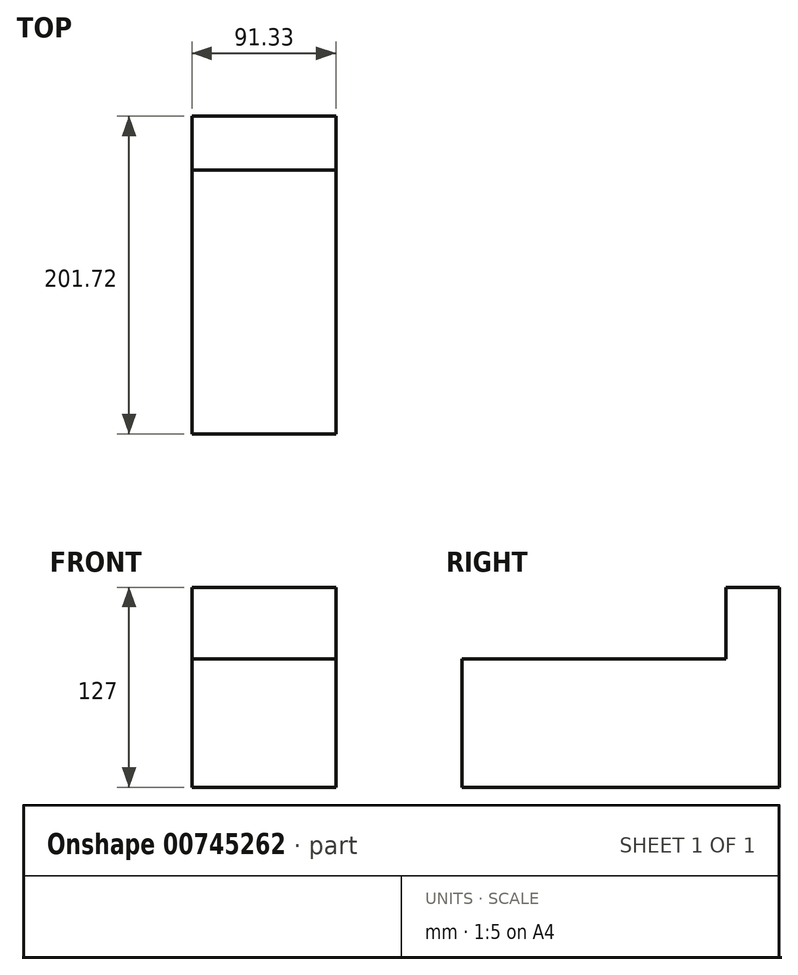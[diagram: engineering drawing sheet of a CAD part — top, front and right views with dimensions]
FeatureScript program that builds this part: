
annotation { "Feature Type Name" : "Feature", "Feature Type Description" : "" }
export const myFeature = defineFeature(function(context is Context, id is Id, definition is map)
    precondition{}
    {
        {
            var Q0;
            Q0=qCreatedBy(makeId("Top.planeOp"),FACE);
            var sketch = newSketch(context, id + "F0", { "sketchPlane" : qUnion([Q0])});
            skLineSegment(sketch, "E0.bottom", {"start": v(-55.85, 45.48) * mm, "end": v(35.48, 45.48) * mm});
            skLineSegment(sketch, "E0.top", {"start": v(-55.85, -52.1) * mm, "end": v(35.48, -52.1) * mm});
            skLineSegment(sketch, "E0.left", {"start": v(-55.85, 45.48) * mm, "end": v(-55.85, -52.1) * mm});
            skLineSegment(sketch, "E0.right", {"start": v(35.48, 45.48) * mm, "end": v(35.48, -52.1) * mm});
            skSolve(sketch);
        }
        {
            var Q0;
            Q0 = qSketchRegion(id + "F0", true);
            extrude(context, id + "F1", {"entities" : qUnion([Q0]), "depth" : 127 * mm, "offsetDistance" : 25.4 * mm});
        }
        {
            var Q0;
            Q0=makeQuery(id+"F1.opExtrude","SWEPT_FACE",FACE,{"disambiguationData":[OSD([sQuery(id+"F0.wireOp",EDGE,"E0.top")])]});
            var sketch = newSketch(context, id + "F2", { "sketchPlane" : qUnion([Q0])});
            skLineSegment(sketch, "E1.bottom", {"start": v(-55.85, 127) * mm, "end": v(35.48, 127) * mm});
            skLineSegment(sketch, "E1.top", {"start": v(-55.85, 81.4) * mm, "end": v(35.48, 81.4) * mm});
            skLineSegment(sketch, "E1.left", {"start": v(-55.85, 127) * mm, "end": v(-55.85, 81.4) * mm});
            skLineSegment(sketch, "E1.right", {"start": v(35.48, 127) * mm, "end": v(35.48, 81.4) * mm});
            skSolve(sketch);
        }
        {
            var Q0;
            Q0 = qSketchRegion(id + "F2", true);
            extrude(context, id + "F3", {"entities" : qUnion([Q0]), "operationType" : NewBodyOperationType.REMOVE, "oppositeDirection" : true, "depth" : 63.5 * mm, "offsetDistance" : 25.4 * mm});
        }
        {
            var Q0;
            Q0=makeQuery(id+"F1.opExtrude","SWEPT_FACE",FACE,{"disambiguationData":[OSD([sQuery(id+"F0.wireOp",EDGE,"E0.top")])]});
            extrude(context, id + "F4", {"entities" : qUnion([Q0]), "operationType" : NewBodyOperationType.ADD, "depth" : 25.4 * mm, "offsetDistance" : 25.4 * mm});
        }
        {
            var Q0;
            Q0=makeQuery(id+"F4.opExtrude","CAP_FACE",FACE,{"disambiguationData":[OSD([sQuery(id+"F0.wireOp",EDGE,"E0.top")])],"isStart":false});
            var sketch = newSketch(context, id + "F5", { "sketchPlane" : qUnion([Q0])});
            skSolve(sketch);
        }
        {
            var Q0;
            {var subQ0=sQuery(id+"F0.wireOp",EDGE,"E0.top");Q0=makeQuery(id+"F5.imprint","IMPRINT",FACE,{"disambiguationData":[TD([[makeQuery(id+"F5.imprint","IMPRINT",EDGE,{"derivedFrom":makeQuery(id+"F4.opExtrude","CAP_EDGE",EDGE,{"disambiguationData":[OSD([subQ0])],"isStart":false})}),1.0]])]});}
            extrude(context, id + "F6", {"entities" : qUnion([Q0]), "operationType" : NewBodyOperationType.ADD, "depth" : 78.74 * mm, "offsetDistance" : 25.4 * mm});
        }
    });
